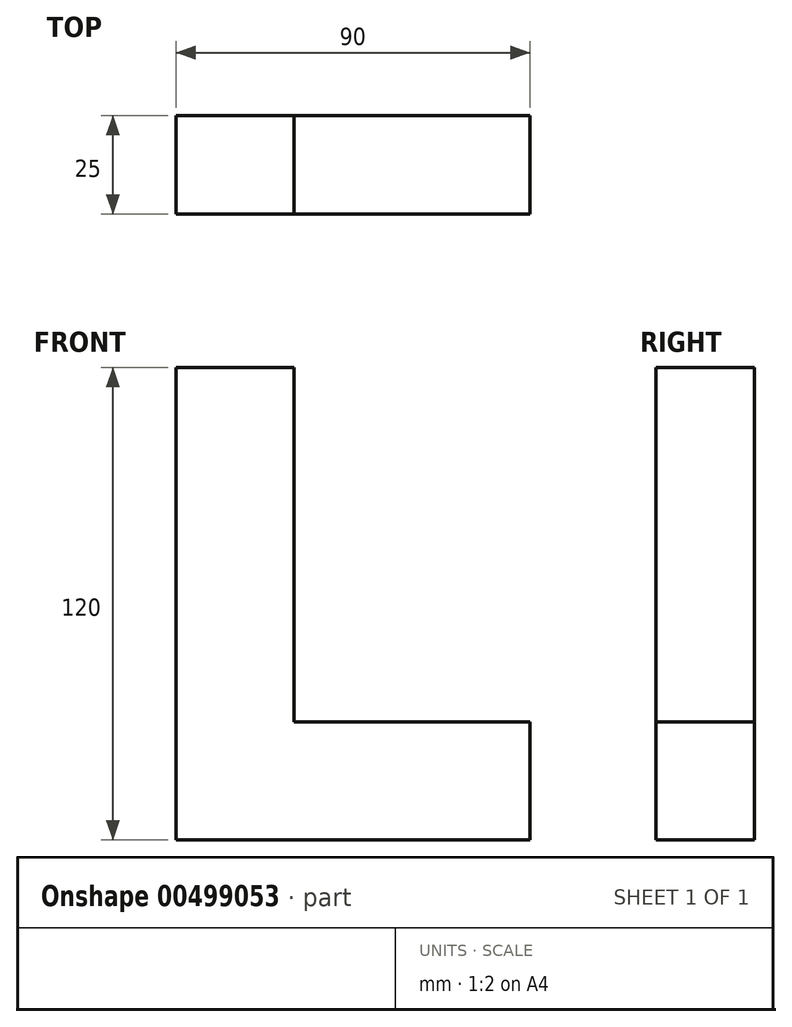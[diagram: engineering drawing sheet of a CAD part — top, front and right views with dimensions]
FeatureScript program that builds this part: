
annotation { "Feature Type Name" : "Feature", "Feature Type Description" : "" }
export const myFeature = defineFeature(function(context is Context, id is Id, definition is map)
    precondition{}
    {
        {
            var Q0;
            Q0=qCreatedBy(makeId("Front.planeOp"),FACE);
            var sketch = newSketch(context, id + "F0", { "sketchPlane" : qUnion([Q0])});
            skLineSegment(sketch, "E0", {"start": v(-61.6, 69) * mm, "end": v(-61.6, -51) * mm});
            skLineSegment(sketch, "E1", {"start": v(-61.6, -51) * mm, "end": v(28.4, -51) * mm});
            skLineSegment(sketch, "E2", {"start": v(28.4, -51) * mm, "end": v(28.4, -21) * mm});
            skLineSegment(sketch, "E3", {"start": v(28.4, -21) * mm, "end": v(-31.6, -21) * mm});
            skLineSegment(sketch, "E4", {"start": v(-31.6, -21) * mm, "end": v(-31.6, 69) * mm});
            skLineSegment(sketch, "E5", {"start": v(-31.6, 69) * mm, "end": v(-61.6, 69) * mm});
            skSolve(sketch);
        }
        {
            var Q0;
            Q0 = qSketchRegion(id + "F0", true);
            extrude(context, id + "F1", {"entities" : qUnion([Q0]), "depth" : 25 * mm});
        }
    });
